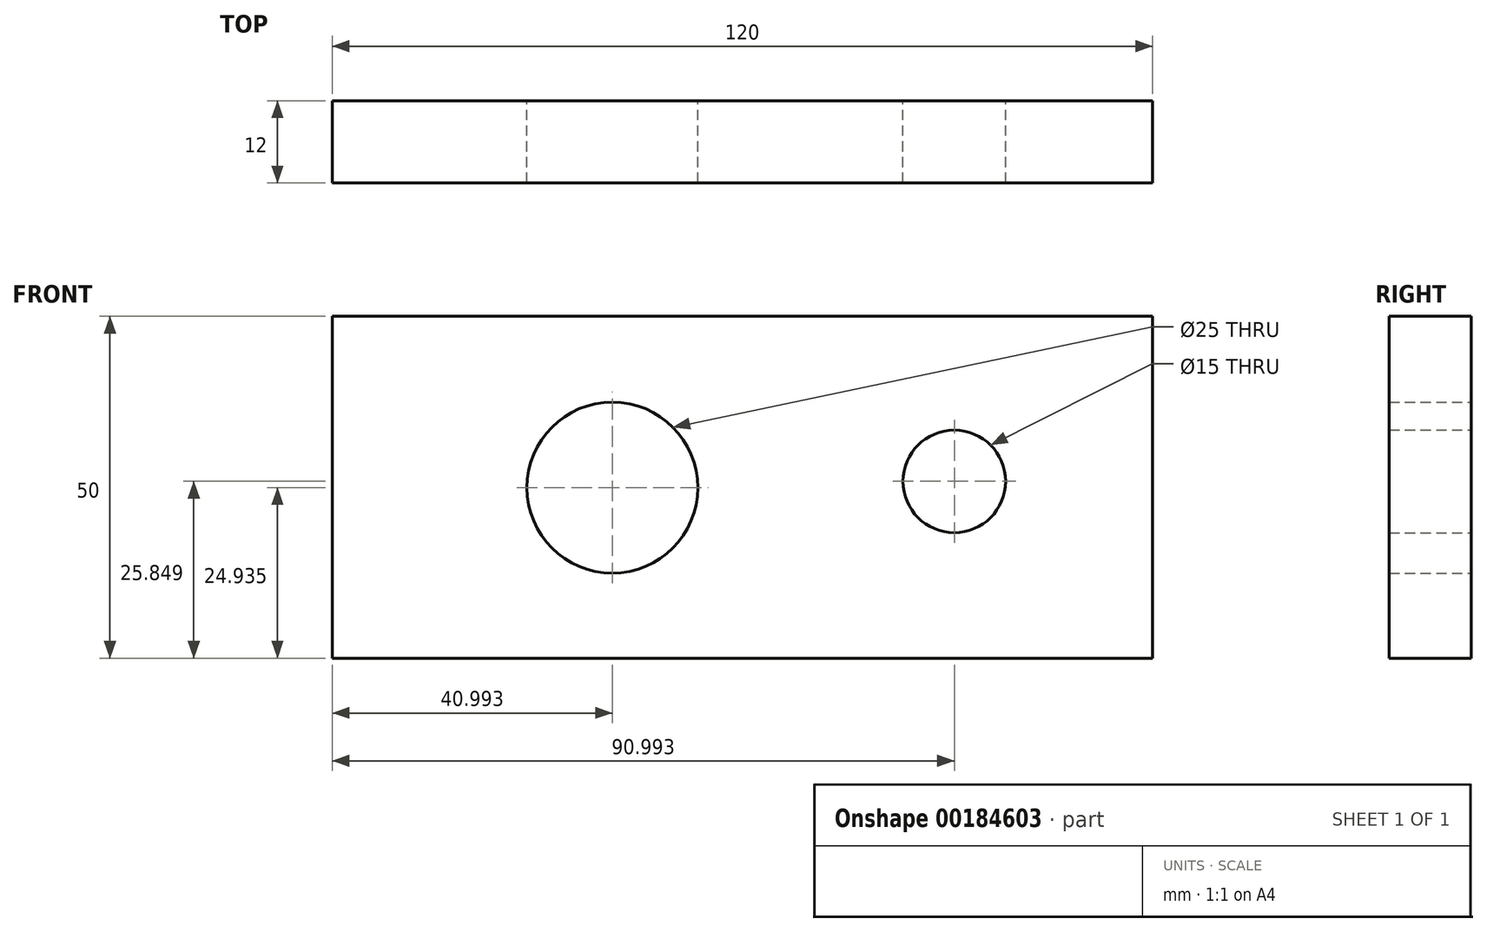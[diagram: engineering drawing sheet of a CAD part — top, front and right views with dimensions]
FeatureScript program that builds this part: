
annotation { "Feature Type Name" : "Feature", "Feature Type Description" : "" }
export const myFeature = defineFeature(function(context is Context, id is Id, definition is map)
    precondition{}
    {
        {
            var Q0;
            Q0=qCreatedBy(makeId("Front.planeOp"),FACE);
            var sketch = newSketch(context, id + "F0", { "sketchPlane" : qUnion([Q0])});
            skLineSegment(sketch, "E0.bottom", {"start": v(-61.1, 27.79) * mm, "end": v(58.9, 27.79) * mm});
            skLineSegment(sketch, "E0.top", {"start": v(-61.1, -22.21) * mm, "end": v(58.9, -22.21) * mm});
            skLineSegment(sketch, "E0.left", {"start": v(-61.1, 27.79) * mm, "end": v(-61.1, -22.21) * mm});
            skLineSegment(sketch, "E0.right", {"start": v(58.9, 27.79) * mm, "end": v(58.9, -22.21) * mm});
            skCircle(sketch, "E1", {"center": v(-20.1, 2.72) * mm, "radius": 12.5 * mm});
            skCircle(sketch, "E2", {"center": v(29.9, 3.64) * mm, "radius": 7.5 * mm});
            skSolve(sketch);
        }
        {
            var Q0;
            Q0=makeQuery(id+"F0.imprint","IMPRINT",FACE,{"disambiguationData":[TD([[makeQuery(id+"F0.imprint","IMPRINT",EDGE,{"derivedFrom":sQuery(id+"F0.wireOp",EDGE,"E0.bottom")}),-1.0]])]});
            extrude(context, id + "F1", {"entities" : qUnion([Q0]), "depth" : 12 * mm});
        }
    });
